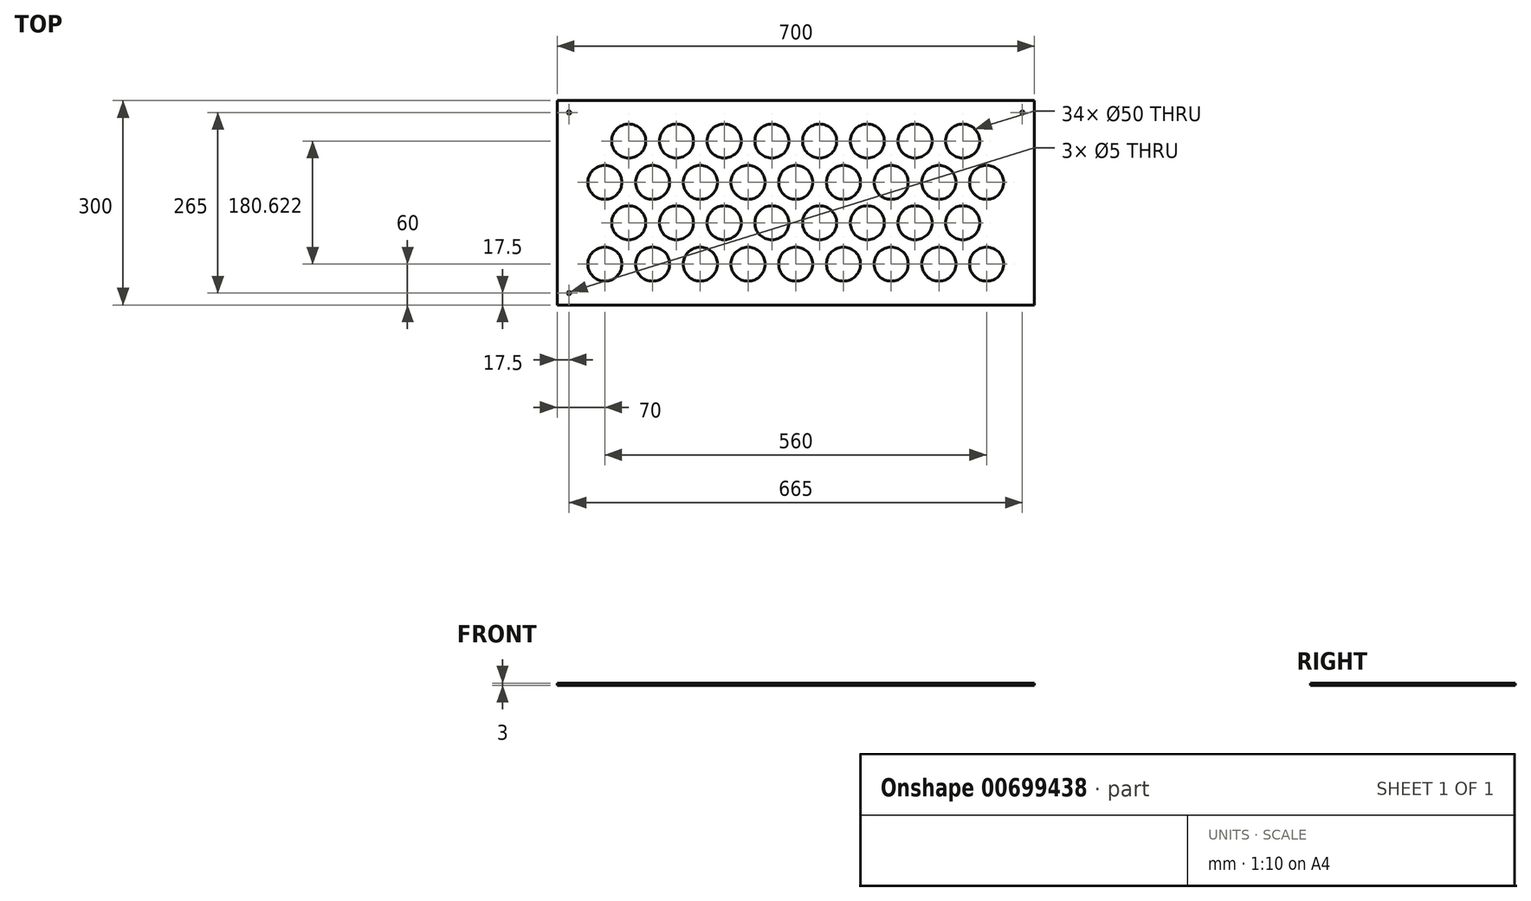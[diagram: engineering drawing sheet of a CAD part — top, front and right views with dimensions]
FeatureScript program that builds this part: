
annotation { "Feature Type Name" : "Feature", "Feature Type Description" : "" }
export const myFeature = defineFeature(function(context is Context, id is Id, definition is map)
    precondition{}
    {
        {
            var Q0;
            Q0=qCreatedBy(makeId("Top.planeOp"),FACE);
            var sketch = newSketch(context, id + "F0", { "sketchPlane" : qUnion([Q0])});
            skLineSegment(sketch, "E0.bottom", {"start": v(-350, 150) * mm, "end": v(350, 150) * mm});
            skLineSegment(sketch, "E0.top", {"start": v(-350, -150) * mm, "end": v(350, -150) * mm});
            skLineSegment(sketch, "E0.left", {"start": v(-350, 150) * mm, "end": v(-350, -150) * mm});
            skLineSegment(sketch, "E0.right", {"start": v(350, 150) * mm, "end": v(350, -150) * mm});
            skPoint(sketch, "E0.middle", {"position": v(0, 0) * mm});
            skCircle(sketch, "E1", {"center": v(-280, -90) * mm, "radius": 25 * mm});
            skCircle(sketch, "E2.1.0.0", {"center": v(-210, -90) * mm, "radius": 25 * mm});
            skCircle(sketch, "E2.2.0.0", {"center": v(-140, -90) * mm, "radius": 25 * mm});
            skCircle(sketch, "E2.3.0.0", {"center": v(-70, -90) * mm, "radius": 25 * mm});
            skCircle(sketch, "E2.4.0.0", {"center": v(0, -90) * mm, "radius": 25 * mm});
            skCircle(sketch, "E2.5.0.0", {"center": v(70, -90) * mm, "radius": 25 * mm});
            skCircle(sketch, "E2.6.0.0", {"center": v(140, -90) * mm, "radius": 25 * mm});
            skCircle(sketch, "E2.7.0.0", {"center": v(210, -90) * mm, "radius": 25 * mm});
            skCircle(sketch, "E2.8.0.0", {"center": v(280, -90) * mm, "radius": 25 * mm});
            skLineSegment(sketch, "E2.direction1", {"start": v(-280, -90) * mm, "end": v(-210, -90) * mm, "construction": true});
            skCircle(sketch, "E3", {"center": v(-245, -29.38) * mm, "radius": 25 * mm});
            skPoint(sketch, "E3.centerSnap0", {"position": v(-245, -90) * mm});
            skLineSegment(sketch, "E4", {"start": v(-245, -90) * mm, "end": v(-245, -29.38) * mm, "construction": true});
            skCircle(sketch, "E5.1.0.0", {"center": v(-175, -29.38) * mm, "radius": 25 * mm});
            skCircle(sketch, "E5.2.0.0", {"center": v(-105, -29.38) * mm, "radius": 25 * mm});
            skCircle(sketch, "E5.3.0.0", {"center": v(-35, -29.38) * mm, "radius": 25 * mm});
            skCircle(sketch, "E5.4.0.0", {"center": v(35, -29.38) * mm, "radius": 25 * mm});
            skCircle(sketch, "E5.5.0.0", {"center": v(105, -29.38) * mm, "radius": 25 * mm});
            skCircle(sketch, "E5.6.0.0", {"center": v(175, -29.38) * mm, "radius": 25 * mm});
            skCircle(sketch, "E5.7.0.0", {"center": v(245, -29.38) * mm, "radius": 25 * mm});
            skLineSegment(sketch, "E5.direction1", {"start": v(-245, -29.38) * mm, "end": v(-175, -29.38) * mm, "construction": true});
            skCircle(sketch, "E6.0.1.0", {"center": v(70, 30) * mm, "radius": 25 * mm});
            skCircle(sketch, "E6.0.1.1", {"center": v(0, 30) * mm, "radius": 25 * mm});
            skCircle(sketch, "E6.0.1.2", {"center": v(-70, 30) * mm, "radius": 25 * mm});
            skCircle(sketch, "E6.0.1.3", {"center": v(-140, 30) * mm, "radius": 25 * mm});
            skCircle(sketch, "E6.0.1.4", {"center": v(35, 90.62) * mm, "radius": 25 * mm});
            skLineSegment(sketch, "E6.0.1.5", {"start": v(-280, 30) * mm, "end": v(-210, 30) * mm, "construction": true});
            skCircle(sketch, "E6.0.1.6", {"center": v(-105, 90.62) * mm, "radius": 25 * mm});
            skCircle(sketch, "E6.0.1.7", {"center": v(-210, 30) * mm, "radius": 25 * mm});
            skCircle(sketch, "E6.0.1.8", {"center": v(-280, 30) * mm, "radius": 25 * mm});
            skCircle(sketch, "E6.0.1.9", {"center": v(175, 90.62) * mm, "radius": 25 * mm});
            skLineSegment(sketch, "E6.0.1.10", {"start": v(-245, 30) * mm, "end": v(-245, 90.62) * mm, "construction": true});
            skCircle(sketch, "E6.0.1.11", {"center": v(-245, 90.62) * mm, "radius": 25 * mm});
            skCircle(sketch, "E6.0.1.12", {"center": v(140, 30) * mm, "radius": 25 * mm});
            skCircle(sketch, "E6.0.1.13", {"center": v(210, 30) * mm, "radius": 25 * mm});
            skCircle(sketch, "E6.0.1.14", {"center": v(280, 30) * mm, "radius": 25 * mm});
            skLineSegment(sketch, "E6.0.1.15", {"start": v(-245, 90.62) * mm, "end": v(-175, 90.62) * mm, "construction": true});
            skCircle(sketch, "E6.0.1.16", {"center": v(245, 90.62) * mm, "radius": 25 * mm});
            skCircle(sketch, "E6.0.1.17", {"center": v(105, 90.62) * mm, "radius": 25 * mm});
            skCircle(sketch, "E6.0.1.18", {"center": v(-35, 90.62) * mm, "radius": 25 * mm});
            skPoint(sketch, "E6.0.1.19", {"position": v(-245, 30) * mm});
            skCircle(sketch, "E6.0.1.20", {"center": v(-175, 90.62) * mm, "radius": 25 * mm});
            skLineSegment(sketch, "E6.direction1", {"start": v(-280, -90) * mm, "end": v(-255, -90) * mm, "construction": true});
            skLineSegment(sketch, "E6.direction2", {"start": v(-280, -90) * mm, "end": v(-280, 30) * mm, "construction": true});
            skCircle(sketch, "E7", {"center": v(-332.5, 132.5) * mm, "radius": 2.5 * mm});
            skCircle(sketch, "E8.MirrorC", {"center": v(332.5, 132.5) * mm, "radius": 2.5 * mm});
            skCircle(sketch, "E9.MirrorC", {"center": v(-332.5, -132.5) * mm, "radius": 2.5 * mm});
            skSolve(sketch);
        }
        {
            var Q0;
            Q0=makeQuery(id+"F0.imprint","IMPRINT",FACE,{"disambiguationData":[TD([[makeQuery(id+"F0.imprint","IMPRINT",EDGE,{"derivedFrom":sQuery(id+"F0.wireOp",EDGE,"E0.bottom")}),-1.0]])]});
            extrude(context, id + "F1", {"entities" : qUnion([Q0]), "depth" : 3 * mm, "offsetDistance" : 25 * mm});
        }
    });
